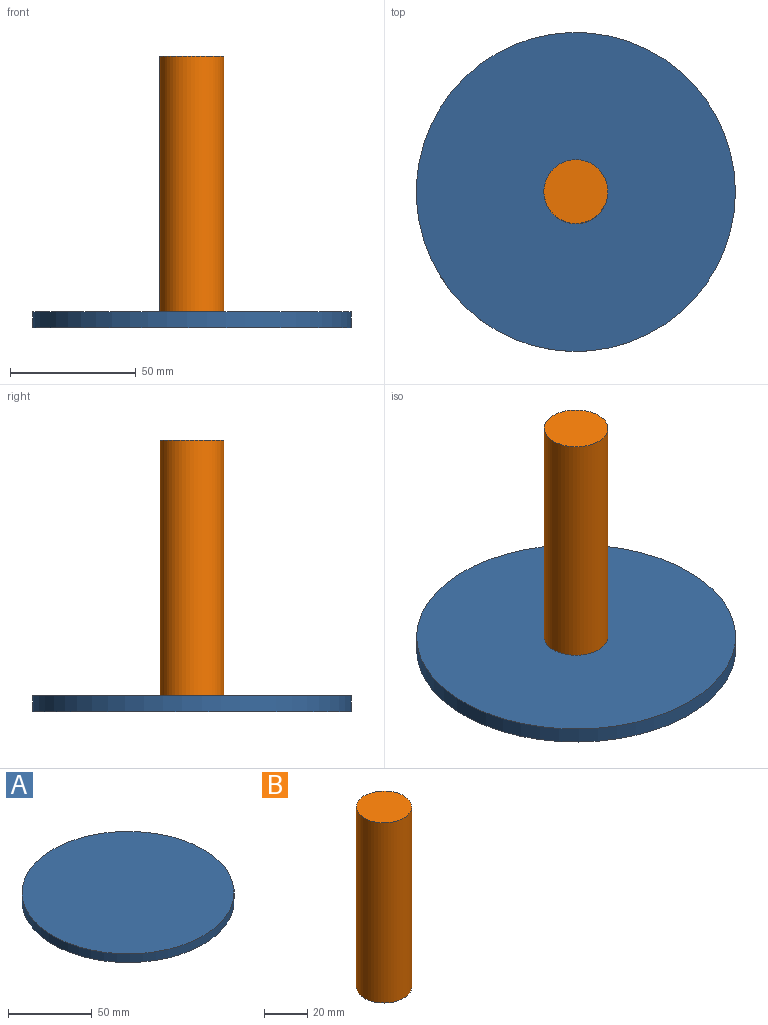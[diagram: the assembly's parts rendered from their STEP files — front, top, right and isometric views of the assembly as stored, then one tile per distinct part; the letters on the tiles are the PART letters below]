
ASSEMBLY  parts=2 mates=2
PART A: 3 faces, bbox 127x127x6.4 mm
  f0: cylinder r=63.5mm len=127mm, axis (0,0,-1), area 2533.5mm2, adj f1,f2
  f1: plane 127x127mm, normal (0,0,1), area 12667.7mm2, adj f0
  f2: plane 127x127mm, normal (0,0,-1), area 12667.7mm2, adj f0
PART B: 3 faces, bbox 25.4x25.4x101.6 mm
  f0: cylinder r=12.7mm len=101.6mm, axis (0,0,-1), area 8107.3mm2, adj f1,f2
  f1: plane 25.4x25.4mm, normal (0,0,1), area 506.7mm2, adj f0
  f2: plane 25.4x25.4mm, normal (0,0,-1), area 506.7mm2, adj f0
PLACE A t=(-55.78,9.6,0)mm
PLACE B t=(-55.78,9.6,6.35)mm
MATE planar A.f0 <-> B.f0  axis (0,0,1) through (-55.78,9.6,6.35)mm
MATE cylindrical A.f0 <-> B.f0  axis (0,0,-1) through (-55.78,9.6,3.18)mm
